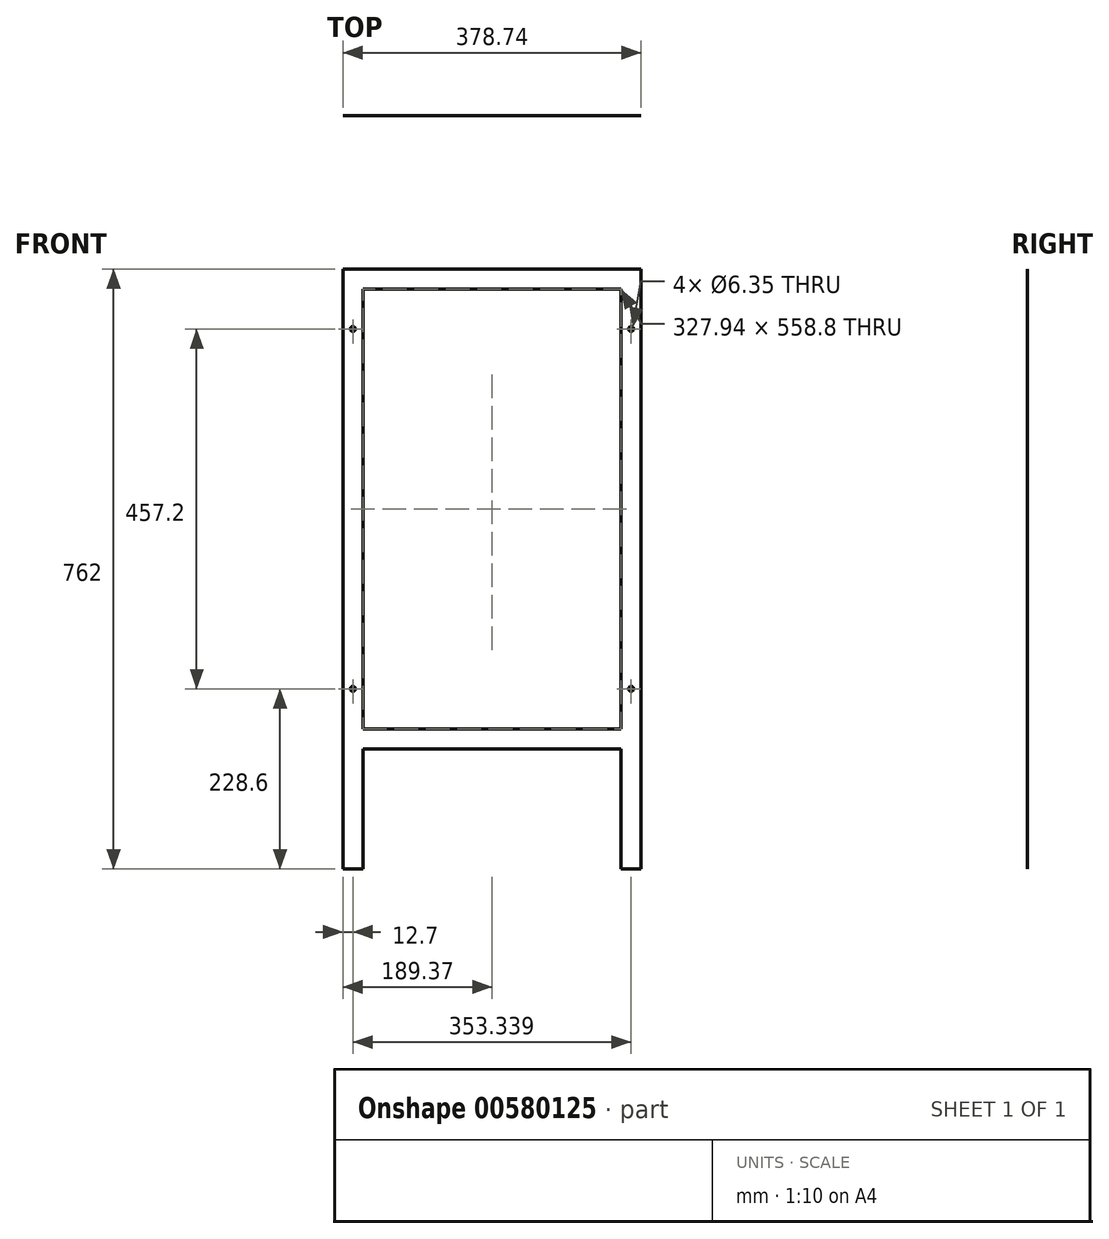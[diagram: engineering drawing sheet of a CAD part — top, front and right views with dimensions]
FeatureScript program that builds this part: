
annotation { "Feature Type Name" : "Feature", "Feature Type Description" : "" }
export const myFeature = defineFeature(function(context is Context, id is Id, definition is map)
    precondition{}
    {
        {
            var Q0;
            Q0=qCreatedBy(makeId("Front.planeOp"),FACE);
            var sketch = newSketch(context, id + "F0", { "sketchPlane" : qUnion([Q0])});
            skLineSegment(sketch, "E0.bottom", {"start": v(189.37, -381) * mm, "end": v(-189.37, -381) * mm});
            skLineSegment(sketch, "E0.top", {"start": v(189.37, 381) * mm, "end": v(-189.37, 381) * mm});
            skLineSegment(sketch, "E0.left", {"start": v(189.37, -381) * mm, "end": v(189.37, 381) * mm});
            skLineSegment(sketch, "E0.right", {"start": v(-189.37, -381) * mm, "end": v(-189.37, 381) * mm});
            skPoint(sketch, "E0.middle", {"position": v(0, 0) * mm});
            skLineSegment(sketch, "E1.bottom", {"start": v(-189.37, 381) * mm, "end": v(189.37, 381) * mm});
            skLineSegment(sketch, "E1.top", {"start": v(-189.37, 370.84) * mm, "end": v(189.37, 370.84) * mm});
            skLineSegment(sketch, "E1.left", {"start": v(-189.37, 381) * mm, "end": v(-189.37, 370.84) * mm});
            skLineSegment(sketch, "E1.right", {"start": v(189.37, 381) * mm, "end": v(189.37, 370.84) * mm});
            skSolve(sketch);
        }
        {
            var Q0;
            Q0=qSketchRegion(id+"F0",true);
            extrude(context, id + "F1", {"entities" : qUnion([Q0]), "depth" : 1 / 254 * mm, "offsetDistance" : 25.4 * mm});
        }
        {
            var Q0;
            Q0=makeQuery(id+"F1.opExtrude","CAP_FACE",FACE,{"disambiguationData":[OSD([sQuery(id+"F0.wireOp",EDGE,"E0.bottom"),sQuery(id+"F0.wireOp",EDGE,"E0.top"),sQuery(id+"F0.wireOp",EDGE,"E0.left"),sQuery(id+"F0.wireOp",EDGE,"E0.right")])],"isStart":false});
            var sketch = newSketch(context, id + "F2", { "sketchPlane" : qUnion([Q0])});
            skLineSegment(sketch, "E2.bottom", {"start": v(-163.97, -228.6) * mm, "end": v(163.97, -228.6) * mm});
            skLineSegment(sketch, "E2.top", {"start": v(-163.97, -381) * mm, "end": v(163.97, -381) * mm});
            skLineSegment(sketch, "E2.left", {"start": v(-163.97, -228.6) * mm, "end": v(-163.97, -381) * mm});
            skLineSegment(sketch, "E2.right", {"start": v(163.97, -228.6) * mm, "end": v(163.97, -381) * mm});
            skLineSegment(sketch, "E3.bottom", {"start": v(-163.97, 355.6) * mm, "end": v(163.97, 355.6) * mm});
            skLineSegment(sketch, "E3.top", {"start": v(-163.97, -203.2) * mm, "end": v(163.97, -203.2) * mm});
            skLineSegment(sketch, "E3.left", {"start": v(-163.97, 355.6) * mm, "end": v(-163.97, -203.2) * mm});
            skLineSegment(sketch, "E3.right", {"start": v(163.97, 355.6) * mm, "end": v(163.97, -203.2) * mm});
            skCircle(sketch, "E4", {"center": v(176.67, 304.8) * mm, "radius": 3.17 * mm});
            skCircle(sketch, "E5", {"center": v(176.67, -152.4) * mm, "radius": 3.17 * mm});
            skCircle(sketch, "E6", {"center": v(-176.67, -152.4) * mm, "radius": 3.17 * mm});
            skCircle(sketch, "E7", {"center": v(-176.67, 304.8) * mm, "radius": 3.18 * mm});
            skLineSegment(sketch, "E8", {"start": v(176.67, 304.8) * mm, "end": v(178.13, 307.62) * mm});
            skLineSegment(sketch, "E9", {"start": v(-176.67, 304.8) * mm, "end": v(-173.5, 304.8) * mm});
            skLineSegment(sketch, "E10", {"start": v(176.67, -152.4) * mm, "end": v(176.67, -149.23) * mm});
            skLineSegment(sketch, "E11", {"start": v(-176.67, -152.4) * mm, "end": v(-176.67, -149.23) * mm});
            skSolve(sketch);
        }
        {
            var Q0;
            Q0=qSketchRegion(id+"F2",true);
            extrude(context, id + "F3", {"entities" : qUnion([Q0]), "operationType" : NewBodyOperationType.REMOVE, "endBound" : BoundingType.THROUGH_ALL, "oppositeDirection" : true, "depth" : 25.4 * mm, "offsetDistance" : 25.4 * mm});
        }
    });
